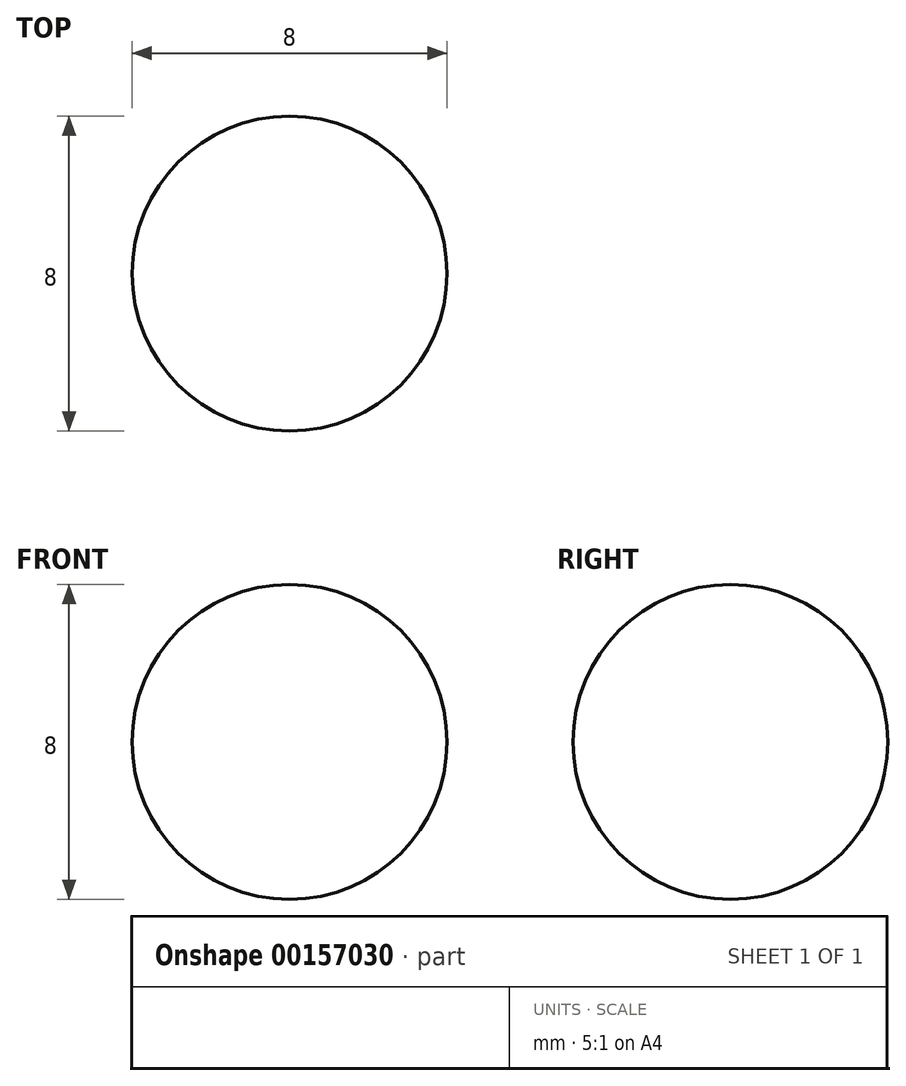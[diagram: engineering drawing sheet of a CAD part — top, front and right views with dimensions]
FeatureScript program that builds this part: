
annotation { "Feature Type Name" : "Feature", "Feature Type Description" : "" }
export const myFeature = defineFeature(function(context is Context, id is Id, definition is map)
    precondition{}
    {
        {
            var Q0;
            Q0=qCreatedBy(makeId("Front.planeOp"),FACE);
            var sketch = newSketch(context, id + "F0", { "sketchPlane" : qUnion([Q0])});
            skArc(sketch, "E0", {"start": v(0, -4) * mm, "mid": v(4, 0) * mm, "end": v(0, 4) * mm});
            skLineSegment(sketch, "E1", {"start": v(0, 4) * mm, "end": v(0, -4) * mm});
            skSolve(sketch);
        }
        {
            var Q0;
            Q0=makeQuery(id+"F0.imprint","IMPRINT",FACE,{"disambiguationData":[TD([[makeQuery(id+"F0.imprint","IMPRINT",EDGE,{"derivedFrom":sQuery(id+"F0.wireOp",EDGE,"E0")}),1.0]])]});
            var Q1;
            Q1=sQuery(id+"F0.wireOp",EDGE,"E1");
            revolve(context, id + "F1", {"entities" : qUnion([Q0]), "axis" : qUnion([Q1]), "revolveType" : RevolveType.FULL});
        }
    });
